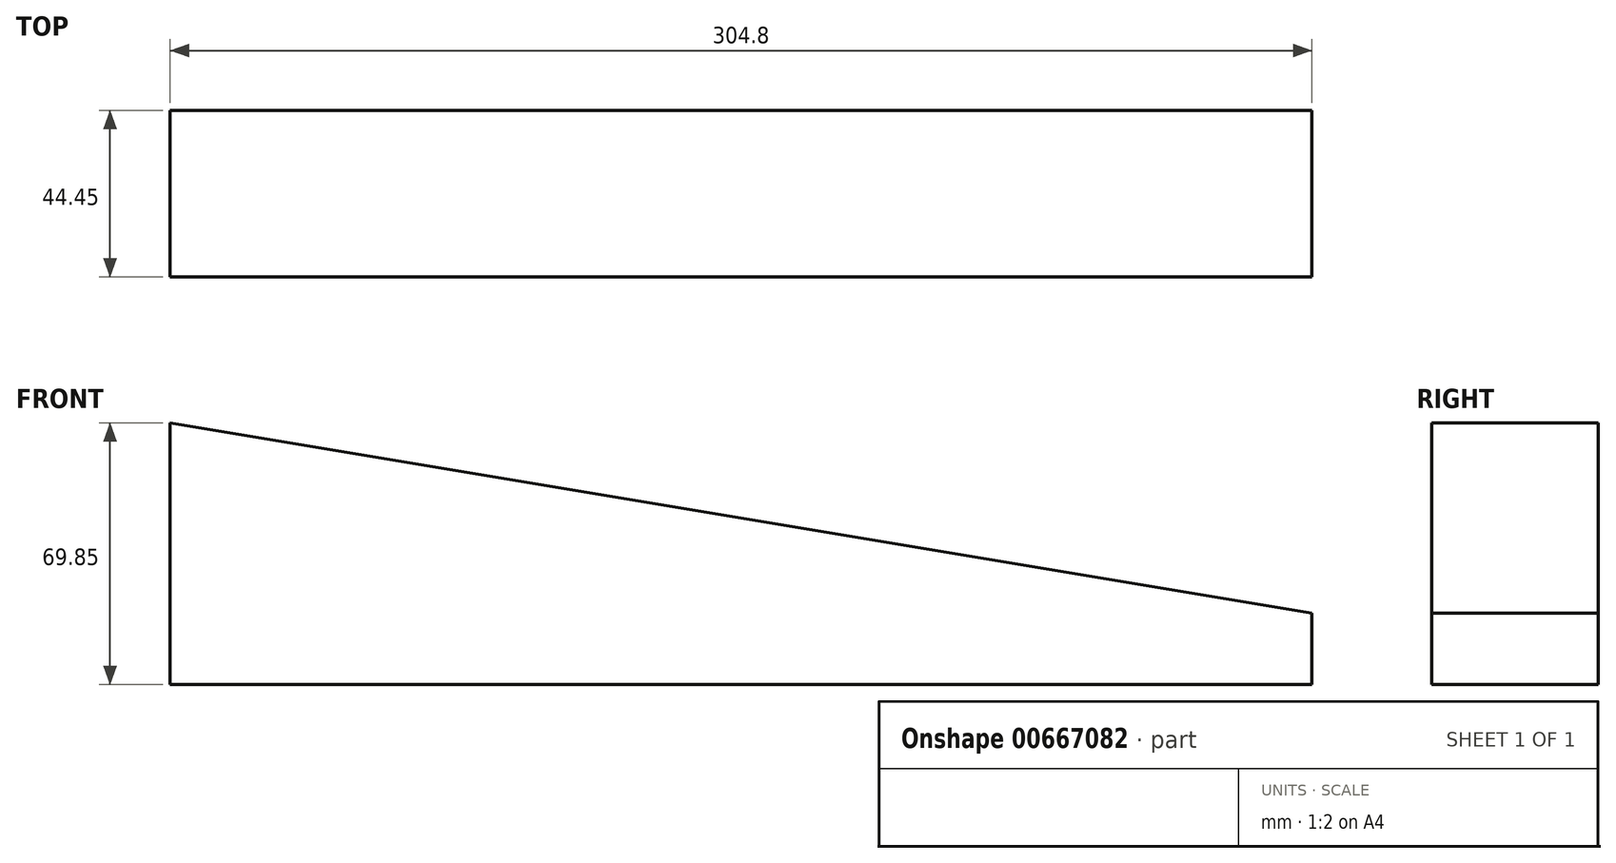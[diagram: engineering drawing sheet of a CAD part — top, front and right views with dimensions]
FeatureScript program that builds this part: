
annotation { "Feature Type Name" : "Feature", "Feature Type Description" : "" }
export const myFeature = defineFeature(function(context is Context, id is Id, definition is map)
    precondition{}
    {
        {
            var Q0;
            Q0=qCreatedBy(makeId("Front.planeOp"),FACE);
            var sketch = newSketch(context, id + "F0", { "sketchPlane" : qUnion([Q0])});
            skLineSegment(sketch, "E0", {"start": v(0, 0) * mm, "end": v(304.8, 0) * mm});
            skLineSegment(sketch, "E1", {"start": v(304.8, 0) * mm, "end": v(304.8, 19.05) * mm});
            skLineSegment(sketch, "E2", {"start": v(304.8, 19.05) * mm, "end": v(0, 69.85) * mm});
            skLineSegment(sketch, "E3", {"start": v(0, 69.85) * mm, "end": v(0, 0) * mm});
            skSolve(sketch);
        }
        {
            var Q0;
            Q0=makeQuery(id+"F0.imprint","IMPRINT",FACE,{"disambiguationData":[TD([[makeQuery(id+"F0.imprint","IMPRINT",EDGE,{"derivedFrom":sQuery(id+"F0.wireOp",EDGE,"E0")}),1.0]])]});
            extrude(context, id + "F1", {"entities" : qUnion([Q0]), "oppositeDirection" : true, "depth" : 44.45 * mm, "offsetDistance" : 25.4 * mm});
        }
    });
